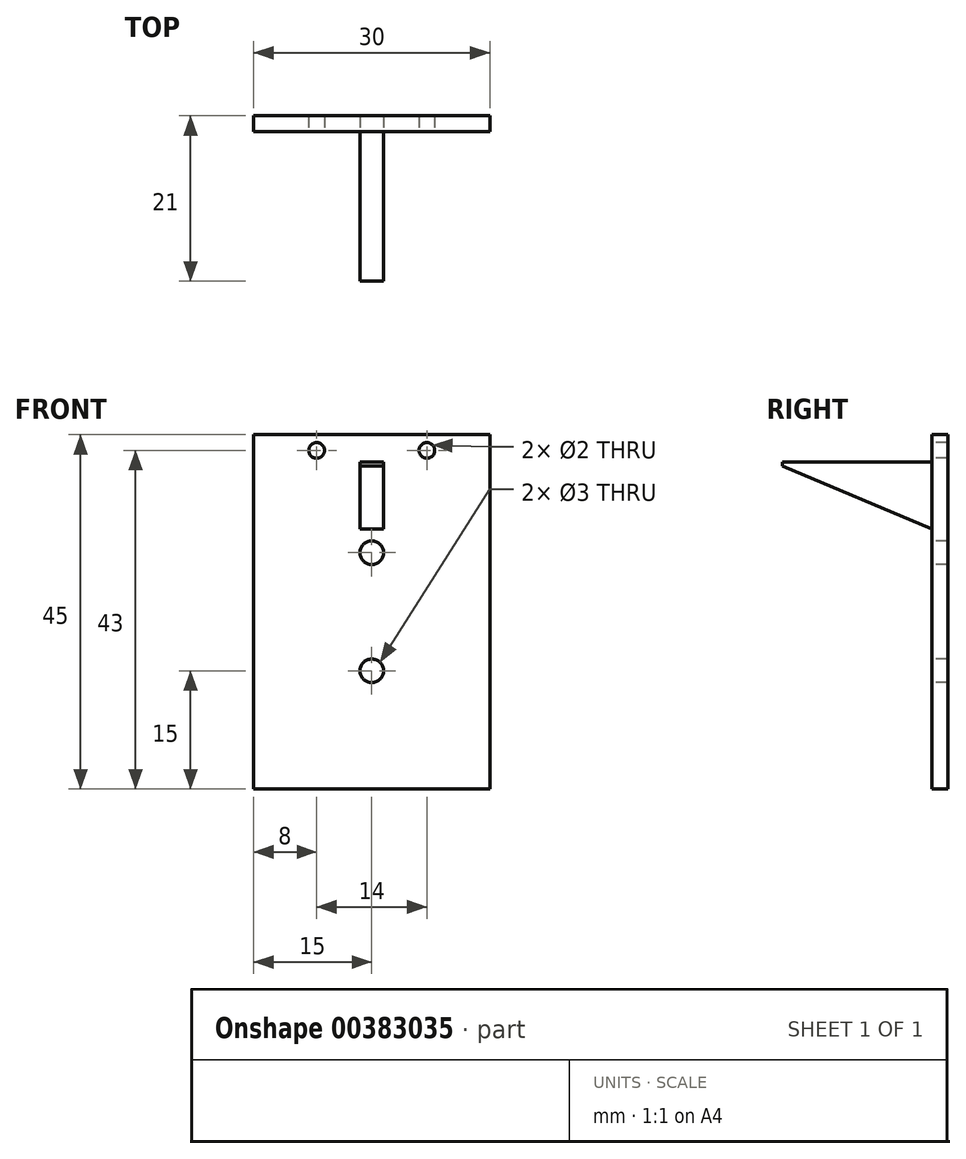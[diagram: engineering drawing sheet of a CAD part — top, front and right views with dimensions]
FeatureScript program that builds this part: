
annotation { "Feature Type Name" : "Feature", "Feature Type Description" : "" }
export const myFeature = defineFeature(function(context is Context, id is Id, definition is map)
    precondition{}
    {
        {
            var Q0;
            Q0=qCreatedBy(makeId("Front.planeOp"),FACE);
            var sketch = newSketch(context, id + "F0", { "sketchPlane" : qUnion([Q0])});
            skLineSegment(sketch, "E0.bottom", {"start": v(-15, 22.5) * mm, "end": v(15, 22.5) * mm});
            skLineSegment(sketch, "E0.top", {"start": v(-15, -22.5) * mm, "end": v(15, -22.5) * mm});
            skLineSegment(sketch, "E0.left", {"start": v(-15, 22.5) * mm, "end": v(-15, -22.5) * mm});
            skLineSegment(sketch, "E0.right", {"start": v(15, 22.5) * mm, "end": v(15, -22.5) * mm});
            skSolve(sketch);
        }
        {
            var Q0;
            Q0=makeQuery(id+"F0.imprint","IMPRINT",FACE,{"disambiguationData":[TD([[makeQuery(id+"F0.imprint","IMPRINT",EDGE,{"derivedFrom":sQuery(id+"F0.wireOp",EDGE,"E0.bottom")}),-1.0]])]});
            extrude(context, id + "F1", {"entities" : qUnion([Q0]), "depth" : 2 * mm});
        }
        {
            var Q0;
            Q0=makeQuery(id+"F1.opExtrude","CAP_FACE",FACE,{"disambiguationData":[OSD([sQuery(id+"F0.wireOp",EDGE,"E0.bottom"),sQuery(id+"F0.wireOp",EDGE,"E0.top"),sQuery(id+"F0.wireOp",EDGE,"E0.left"),sQuery(id+"F0.wireOp",EDGE,"E0.right")])],"isStart":false});
            var sketch = newSketch(context, id + "F2", { "sketchPlane" : qUnion([Q0])});
            skPoint(sketch, "E1", {"position": v(-7, 20.5) * mm});
            skPoint(sketch, "E2", {"position": v(7, 20.5) * mm});
            skPoint(sketch, "E3", {"position": v(0, 7.5) * mm});
            skPoint(sketch, "E4", {"position": v(0, -7.5) * mm});
            skLineSegment(sketch, "E5", {"start": v(-1.5, 19) * mm, "end": v(-1.5, 10.5) * mm});
            skLineSegment(sketch, "E6", {"start": v(-1.5, 10.5) * mm, "end": v(1.5, 10.5) * mm});
            skLineSegment(sketch, "E7", {"start": v(1.5, 10.5) * mm, "end": v(1.5, 19) * mm});
            skLineSegment(sketch, "E8", {"start": v(-1.5, 19) * mm, "end": v(1.5, 19) * mm});
            skSolve(sketch);
        }
        {
            var Q0;
            Q0=sQuery(id+"F2.wireOp",VERTEX,"E1");
            var Q1;
            Q1=sQuery(id+"F2.wireOp",VERTEX,"E2");
            var Q2;
            Q2=makeQuery(id+"F1.opExtrude","SWEPT_BODY",BODY,{"disambiguationData":[OSD([sQuery(id+"F0.wireOp",EDGE,"E0.bottom"),sQuery(id+"F0.wireOp",EDGE,"E0.top"),sQuery(id+"F0.wireOp",EDGE,"E0.left"),sQuery(id+"F0.wireOp",EDGE,"E0.right")])]});
            hole(context, id + "F3", {"style" : HoleStyle.SIMPLE, "endStyle" : HoleEndStyle.THROUGH, "holeDiameter" : 2 * mm, "isTappedThrough" : true, "tappedDepth" : 12.7 * mm, "tapClearance" : 3, "locations" : qUnion([Q0, Q1]), "scope" : qUnion([Q2])});
        }
        {
            var Q0;
            Q0=sQuery(id+"F2.wireOp",VERTEX,"E3");
            var Q1;
            Q1=sQuery(id+"F2.wireOp",VERTEX,"E4");
            var Q2;
            Q2=makeQuery(id+"F1.opExtrude","SWEPT_BODY",BODY,{"disambiguationData":[OSD([sQuery(id+"F0.wireOp",EDGE,"E0.bottom"),sQuery(id+"F0.wireOp",EDGE,"E0.top"),sQuery(id+"F0.wireOp",EDGE,"E0.left"),sQuery(id+"F0.wireOp",EDGE,"E0.right")])]});
            hole(context, id + "F4", {"style" : HoleStyle.SIMPLE, "endStyle" : HoleEndStyle.THROUGH, "holeDiameter" : 3 * mm, "isTappedThrough" : true, "tappedDepth" : 12.7 * mm, "tapClearance" : 3, "locations" : qUnion([Q0, Q1]), "scope" : qUnion([Q2])});
        }
        {
            var Q0;
            Q0=makeQuery(id+"F2.imprint","IMPRINT",FACE,{"disambiguationData":[TD([[makeQuery(id+"F2.imprint","IMPRINT",EDGE,{"derivedFrom":sQuery(id+"F2.wireOp",EDGE,"E5")}),1.0]])]});
            extrude(context, id + "F5", {"entities" : qUnion([Q0]), "operationType" : NewBodyOperationType.ADD, "depth" : 19 * mm});
        }
        {
            var Q0;
            Q0=makeQuery(id+"F5.opExtrude","CAP_EDGE",EDGE,{"disambiguationData":[OSD([sQuery(id+"F2.wireOp",EDGE,"E6")])],"isStart":false});
            chamfer(context, id + "F6", {"entities" : qUnion([Q0]), "chamferType" : ChamferType.TWO_OFFSETS, "width1" : 8 * mm, "oppositeDirection" : false, "width2" : 19 * mm, "tangentPropagation" : true});
        }
    });
